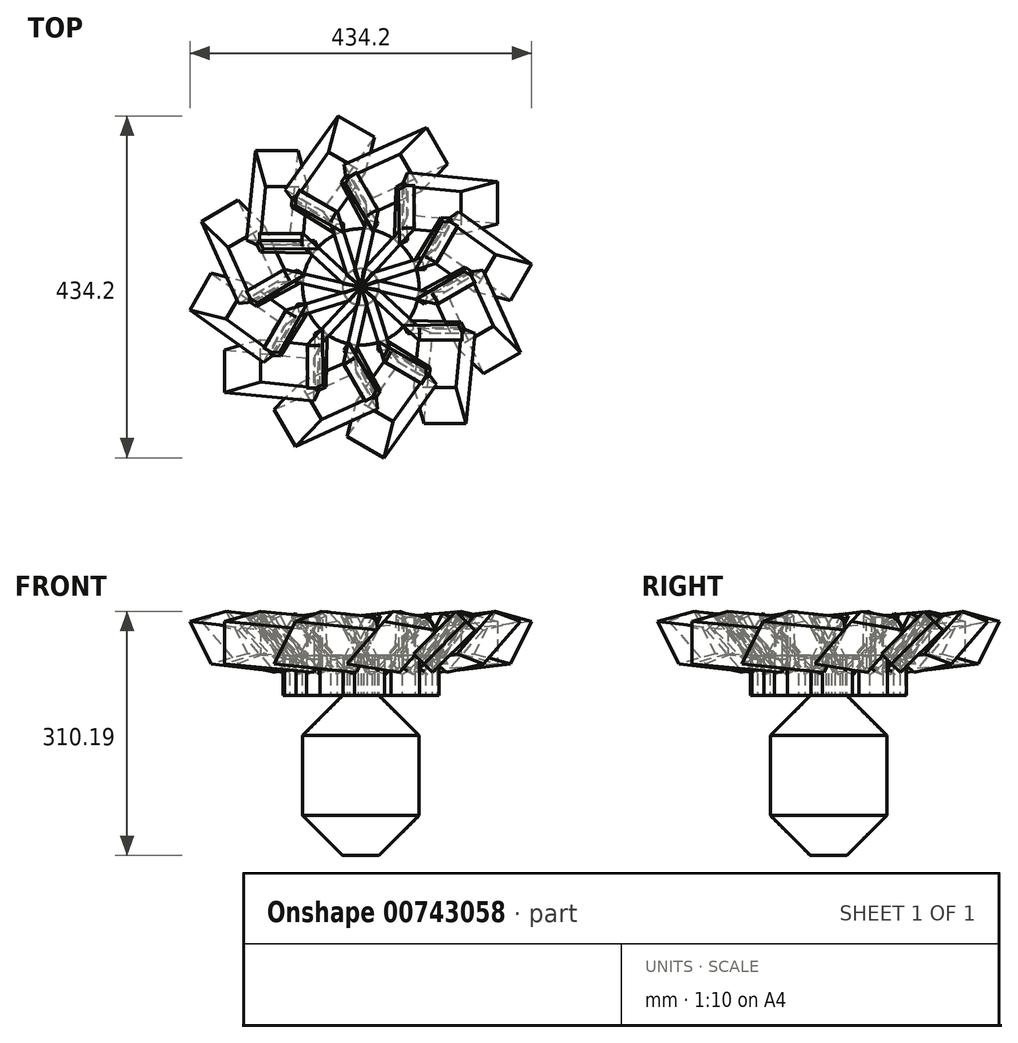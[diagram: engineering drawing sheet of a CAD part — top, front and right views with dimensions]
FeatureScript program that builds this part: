
annotation { "Feature Type Name" : "Feature", "Feature Type Description" : "" }
export const myFeature = defineFeature(function(context is Context, id is Id, definition is map)
    precondition{}
    {
        {
            var Q0;
            Q0=qCreatedBy(makeId("Top.planeOp"),FACE);
            var sketch = newSketch(context, id + "F0", { "sketchPlane" : qUnion([Q0])});
            skCircle(sketch, "E0", {"center": v(0, 0) * mm, "radius": 73.9 * mm});
            skSolve(sketch);
        }
        {
            var Q0;
            Q0=makeQuery(id+"F0.imprint","IMPRINT",FACE,{"disambiguationData":[TD([[makeQuery(id+"F0.imprint","IMPRINT",EDGE,{"derivedFrom":sQuery(id+"F0.wireOp",EDGE,"E0")}),1.0]])]});
            extrude(context, id + "F1", {"entities" : qUnion([Q0]), "depth" : 101.6 * mm, "offsetDistance" : 25.4 * mm});
        }
        {
            var Q0;
            Q0=makeQuery(id+"F1.opExtrude","SWEPT_BODY",BODY,{"disambiguationData":[OSD([sQuery(id+"F0.wireOp",EDGE,"E0")])]});
            var Q1;
            Q1=makeQuery(id+"F1.opExtrude","CAP_FACE",FACE,{"disambiguationData":[OSD([sQuery(id+"F0.wireOp",EDGE,"E0")])],"isStart":true});
            mirror(context, id + "F2", {"operationType" : NewBodyOperationType.ADD, "entities" : qUnion([Q0]), "mirrorPlane" : qUnion([Q1])});
        }
        {
            var Q0;
            Q0=makeQuery(id+"F2.opPattern","COPY",EDGE,{"derivedFrom":makeQuery(id+"F1.opExtrude","CAP_EDGE",EDGE,{"disambiguationData":[OSD([sQuery(id+"F0.wireOp",EDGE,"E0")])],"isStart":false}),"instanceName":"1"});
            chamfer(context, id + "F3", {"entities" : qUnion([Q0]), "width" : 50.8 * mm, "tangentPropagation" : true});
        }
        {
            var Q0;
            Q0=makeQuery(id+"F1.opExtrude","CAP_EDGE",EDGE,{"disambiguationData":[OSD([sQuery(id+"F0.wireOp",EDGE,"E0")])],"isStart":false});
            chamfer(context, id + "F4", {"entities" : qUnion([Q0]), "width" : 50.8 * mm, "tangentPropagation" : true});
        }
        {
            var Q0;
            Q0=makeQuery(id+"F1.opExtrude","CAP_FACE",FACE,{"disambiguationData":[OSD([sQuery(id+"F0.wireOp",EDGE,"E0")])],"isStart":false});
            cPlane(context, id + "F5", {"entities" : qUnion([Q0]), "cplaneType" : CPlaneType.OFFSET, "offset" : 0 * mm, "width" : 152.4 * mm, "height" : 152.4 * mm});
        }
        {
            var Q0;
            Q0=qCreatedBy(id+"F5.planeOp",FACE);
            var sketch = newSketch(context, id + "F6", { "sketchPlane" : qUnion([Q0])});
            skLineSegment(sketch, "E1", {"start": v(0, 0) * mm, "end": v(-74.54, 69.03) * mm});
            skLineSegment(sketch, "E2", {"start": v(-74.54, 69.03) * mm, "end": v(-74.54, 52.07) * mm});
            skLineSegment(sketch, "E3", {"start": v(-74.54, 52.07) * mm, "end": v(-22.26, 3.65) * mm});
            skLineSegment(sketch, "E4", {"start": v(-22.26, 3.65) * mm, "end": v(0, 0) * mm});
            skSolve(sketch);
        }
        {
            var Q0;
            Q0=makeQuery(id+"F6.imprint","IMPRINT",FACE,{"disambiguationData":[TD([[makeQuery(id+"F6.imprint","IMPRINT",EDGE,{"derivedFrom":sQuery(id+"F6.wireOp",EDGE,"E1")}),1.0]])]});
            extrude(context, id + "F7", {"entities" : qUnion([Q0]), "operationType" : NewBodyOperationType.ADD, "depth" : 50.8 * mm, "offsetDistance" : 25.4 * mm});
        }
        {
            var Q0;
            Q0=makeQuery(id+"F7.opExtrude","SWEPT_BODY",BODY,{"disambiguationData":[OSD([sQuery(id+"F6.wireOp",EDGE,"E1"),sQuery(id+"F6.wireOp",EDGE,"E2"),sQuery(id+"F6.wireOp",EDGE,"E3"),sQuery(id+"F6.wireOp",EDGE,"E4")])]});
            var Q1;
            Q1=makeQuery(id+"F1.opExtrude","SWEPT_BODY",BODY,{"disambiguationData":[OSD([sQuery(id+"F0.wireOp",EDGE,"E0")])]});
            var Q2;
            Q2=makeQuery(id+"F4.opChamfer","BLEND_FACE",FACE,{"disambiguationData":[OSD([sQuery(id+"F0.wireOp",EDGE,"E0")])]});
            circularPattern(context, id + "F8", {"entities" : qUnion([Q0, Q1]), "axis" : qUnion([Q2]), "angle" : 360 * degree, "instanceCount" : 12, "equalSpace" : true});
        }
        {
            var Q0;
            Q0=makeQuery(id+"F8.opPattern","COPY",EDGE,{"derivedFrom":makeQuery(id+"F7.opExtrude","CAP_EDGE",EDGE,{"disambiguationData":[OSD([sQuery(id+"F6.wireOp",EDGE,"E2")])],"isStart":false}),"instanceName":"7"});
            chamfer(context, id + "F9", {"entities" : qUnion([Q0]), "width" : 5.08 * mm, "tangentPropagation" : true});
        }
        {
            var Q0;
            Q0=makeQuery(id+"F9.opChamfer","BLEND_FACE",FACE,{"disambiguationData":[OSD([sQuery(id+"F6.wireOp",EDGE,"E2")])]});
            var sketch = newSketch(context, id + "F10", { "sketchPlane" : qUnion([Q0])});
            skLineSegment(sketch, "E5", {"start": v(-72.8, -7.79) * mm, "end": v(-128.62, -59.65) * mm});
            skLineSegment(sketch, "E6", {"start": v(-128.62, -59.65) * mm, "end": v(-143.57, -106.63) * mm});
            skLineSegment(sketch, "E7", {"start": v(-143.57, -106.63) * mm, "end": v(-59.14, -28.2) * mm});
            skLineSegment(sketch, "E8", {"start": v(-59.14, -28.2) * mm, "end": v(-72.8, -7.79) * mm});
            skSolve(sketch);
        }
        {
            var Q0;
            {var subQ0=sQuery(id+"F10.wireOp",EDGE,"E6");Q0=makeQuery(id+"F10.imprint","IMPRINT",FACE,{"disambiguationData":[TD([[makeQuery(id+"F10.imprint","IMPRINT",EDGE,{"derivedFrom":subQ0}),1.0]])]});}
            extrude(context, id + "F11", {"entities" : qUnion([Q0]), "depth" : 76.2 * mm, "offsetDistance" : 25.4 * mm});
        }
        {
            var Q0;
            Q0=makeQuery(id+"F11.opExtrude","SWEPT_BODY",BODY,{"disambiguationData":[OSD([sQuery(id+"F6.wireOp",EDGE,"E1"),sQuery(id+"F6.wireOp",EDGE,"E2"),sQuery(id+"F10.wireOp",EDGE,"E5"),sQuery(id+"F10.wireOp",EDGE,"E6"),sQuery(id+"F10.wireOp",EDGE,"E7"),sQuery(id+"F10.wireOp",EDGE,"E8")])]});
            var Q1;
            Q1=makeQuery(id+"F4.opChamfer","BLEND_FACE",FACE,{"disambiguationData":[OSD([sQuery(id+"F0.wireOp",EDGE,"E0")])]});
            circularPattern(context, id + "F12", {"entities" : qUnion([Q0]), "axis" : qUnion([Q1]), "angle" : 360 * degree, "instanceCount" : 12, "equalSpace" : true});
        }
        {
            var Q0;
            Q0=makeQuery(id+"F12.opPattern","COPY",EDGE,{"derivedFrom":makeQuery(id+"F11.opExtrude","SWEPT_EDGE",EDGE,{"disambiguationData":[OSD([sQuery(id+"F6.wireOp",EDGE,"E2"),sQuery(id+"F6.wireOp",EDGE,"E3"),sQuery(id+"F10.wireOp",EDGE,"E5"),sQuery(id+"F10.wireOp",EDGE,"E8")])]}),"instanceName":"5"});
            chamfer(context, id + "F13", {"entities" : qUnion([Q0]), "width" : 5.08 * mm, "tangentPropagation" : true});
        }
        {
            var Q0;
            Q0=makeQuery(id+"F13.opChamfer","BLEND_FACE",FACE,{"disambiguationData":[OSD([sQuery(id+"F6.wireOp",EDGE,"E2"),sQuery(id+"F6.wireOp",EDGE,"E3"),sQuery(id+"F10.wireOp",EDGE,"E5"),sQuery(id+"F10.wireOp",EDGE,"E8")])]});
            var sketch = newSketch(context, id + "F14", { "sketchPlane" : qUnion([Q0])});
            skLineSegment(sketch, "E9", {"start": v(-138.23, 200.06) * mm, "end": v(-66.1, 138.07) * mm});
            skLineSegment(sketch, "E10", {"start": v(-57.33, 144.37) * mm, "end": v(-134.44, 204.77) * mm});
            skLineSegment(sketch, "E11", {"start": v(-134.44, 204.77) * mm, "end": v(-138.23, 200.06) * mm});
            skLineSegment(sketch, "E12", {"start": v(-57.33, 144.37) * mm, "end": v(-66.1, 138.07) * mm});
            skSolve(sketch);
        }
        {
            var Q0;
            Q0=makeQuery(id+"F14.imprint","IMPRINT",FACE,{"disambiguationData":[TD([[makeQuery(id+"F14.imprint","IMPRINT",EDGE,{"derivedFrom":sQuery(id+"F14.wireOp",EDGE,"E10")}),1.0]])]});
            var Q1;
            {var subQ0=sQuery(id+"F14.wireOp",EDGE,"E11");Q1=makeQuery(id+"F14.imprint","IMPRINT",FACE,{"disambiguationData":[TD([[makeQuery(id+"F14.imprint","IMPRINT",EDGE,{"derivedFrom":subQ0}),-1.0]])]});}
            extrude(context, id + "F15", {"entities" : qUnion([Q0, Q1]), "depth" : 12.7 * mm, "offsetDistance" : 25.4 * mm});
        }
        {
            var Q0;
            Q0=makeQuery(id+"F15.opExtrude","SWEPT_BODY",BODY,{"disambiguationData":[OSD([sQuery(id+"F14.wireOp",EDGE,"E9"),sQuery(id+"F14.wireOp",EDGE,"E10"),sQuery(id+"F14.wireOp",EDGE,"E12"),sQuery(id+"F14.wireOp",EDGE,"E11")])]});
            var Q1;
            {var subQ0=makeQuery(id+"F1.opExtrude","SWEPT_FACE",FACE,{"disambiguationData":[OSD([sQuery(id+"F0.wireOp",EDGE,"E0")])]});Q1=makeQuery(id+"F2.boolean.opBoolean","MERGE",FACE,{"derivedFrom":[subQ0,makeQuery(id+"F2.opPattern","COPY",FACE,{"derivedFrom":subQ0,"instanceName":"1"})]});}
            circularPattern(context, id + "F16", {"entities" : qUnion([Q0]), "axis" : qUnion([Q1]), "angle" : 360 * degree, "instanceCount" : 12, "equalSpace" : true});
        }
    });
